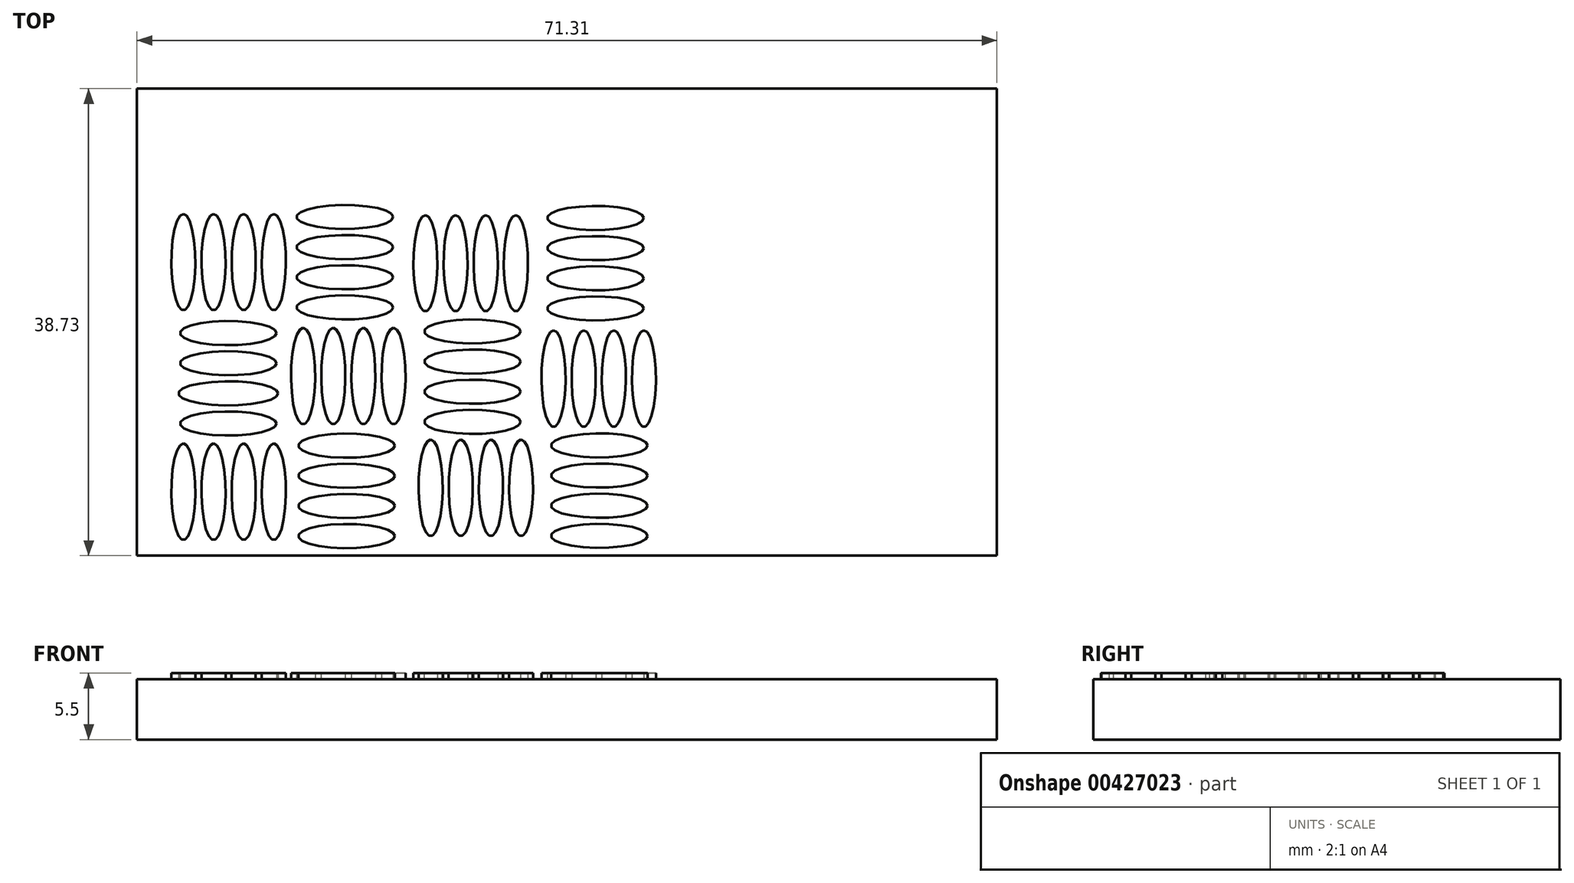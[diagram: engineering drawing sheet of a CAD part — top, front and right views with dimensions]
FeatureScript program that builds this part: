
annotation { "Feature Type Name" : "Feature", "Feature Type Description" : "" }
export const myFeature = defineFeature(function(context is Context, id is Id, definition is map)
    precondition{}
    {
        {
            var Q0;
            Q0=qCreatedBy(makeId("Top.planeOp"),FACE);
            var sketch = newSketch(context, id + "F0", { "sketchPlane" : qUnion([Q0])});
            skLineSegment(sketch, "E0.bottom", {"start": v(0, -0.64) * mm, "end": v(71.3, -0.64) * mm});
            skLineSegment(sketch, "E0.top", {"start": v(0, 38.1) * mm, "end": v(71.3, 38.1) * mm});
            skLineSegment(sketch, "E0.left", {"start": v(0, -0.64) * mm, "end": v(0, 38.1) * mm});
            skLineSegment(sketch, "E0.right", {"start": v(71.3, -0.64) * mm, "end": v(71.3, 38.1) * mm});
            skSolve(sketch);
        }
        {
            var Q0;
            Q0 = qSketchRegion(id + "F0", true);
            extrude(context, id + "F1", {"entities" : qUnion([Q0]), "depth" : 5 * mm});
        }
        {
            var Q0;
            Q0=makeQuery(id+"F1.opExtrude","CAP_FACE",FACE,{"disambiguationData":[OSD([sQuery(id+"F0.wireOp",EDGE,"E0.bottom"),sQuery(id+"F0.wireOp",EDGE,"E0.top"),sQuery(id+"F0.wireOp",EDGE,"E0.left"),sQuery(id+"F0.wireOp",EDGE,"E0.right")])],"isStart":false});
            var sketch = newSketch(context, id + "F2", { "sketchPlane" : qUnion([Q0])});
            skEllipse(sketch, "E1", {"center": v(3.85, 4.66) * mm, "majorRadius": 4 * mm, "minorRadius": 1 * mm, "majorAxis": v(0, 1)});
            skEllipse(sketch, "E2", {"center": v(6.35, 4.66) * mm, "majorRadius": 4 * mm, "minorRadius": 1 * mm, "majorAxis": v(0, 1)});
            skPoint(sketch, "E2.centerSnap0", {"position": v(4.85, 4.66) * mm});
            skEllipse(sketch, "E3", {"center": v(8.85, 4.66) * mm, "majorRadius": 4 * mm, "minorRadius": 1 * mm, "majorAxis": v(0, 1)});
            skEllipse(sketch, "E4", {"center": v(11.35, 4.66) * mm, "majorRadius": 4 * mm, "minorRadius": 1 * mm, "majorAxis": v(0, 1)});
            skEllipse(sketch, "E5", {"center": v(7.57, 10.32) * mm, "majorRadius": 4 * mm, "minorRadius": 1 * mm, "majorAxis": v(1, 0)});
            skEllipse(sketch, "E6", {"center": v(7.57, 12.82) * mm, "majorRadius": 4.13 * mm, "minorRadius": 1 * mm, "majorAxis": v(1, 0)});
            skEllipse(sketch, "E7", {"center": v(7.57, 15.32) * mm, "majorRadius": 4 * mm, "minorRadius": 1 * mm, "majorAxis": v(1, 0)});
            skEllipse(sketch, "E8", {"center": v(7.57, 17.82) * mm, "majorRadius": 4 * mm, "minorRadius": 1 * mm, "majorAxis": v(1, 0)});
            skPoint(sketch, "E8.centerSnap0", {"position": v(7.57, 16.32) * mm});
            skSolve(sketch);
        }
        {
            var Q0;
            Q0 = qSketchRegion(id + "F2", true);
            extrude(context, id + "F3", {"entities" : qUnion([Q0]), "operationType" : NewBodyOperationType.ADD, "depth" : 0.5 * mm});
        }
        {
            var Q0;
            Q0=makeQuery(id+"F1.opExtrude","CAP_FACE",FACE,{"disambiguationData":[OSD([sQuery(id+"F0.wireOp",EDGE,"E0.bottom"),sQuery(id+"F0.wireOp",EDGE,"E0.top"),sQuery(id+"F0.wireOp",EDGE,"E0.left"),sQuery(id+"F0.wireOp",EDGE,"E0.right")])],"isStart":false});
            var sketch = newSketch(context, id + "F4", { "sketchPlane" : qUnion([Q0])});
            skEllipse(sketch, "E9", {"center": v(3.85, 23.7) * mm, "majorRadius": 4 * mm, "minorRadius": 1 * mm, "majorAxis": v(0, 1)});
            skPoint(sketch, "E9.centerSnap0", {"position": v(3.85, 8.66) * mm});
            skEllipse(sketch, "E10", {"center": v(6.35, 23.7) * mm, "majorRadius": 4 * mm, "minorRadius": 1 * mm, "majorAxis": v(0, 1)});
            skPoint(sketch, "E10.centerSnap0", {"position": v(4.85, 23.7) * mm});
            skEllipse(sketch, "E11", {"center": v(8.85, 23.7) * mm, "majorRadius": 4 * mm, "minorRadius": 1 * mm, "majorAxis": v(0, 1)});
            skPoint(sketch, "E11.centerSnap0", {"position": v(7.35, 23.7) * mm});
            skEllipse(sketch, "E12", {"center": v(11.35, 23.7) * mm, "majorRadius": 4 * mm, "minorRadius": 1 * mm, "majorAxis": v(0, 1)});
            skEllipse(sketch, "E13", {"center": v(17.39, 0.99) * mm, "majorRadius": 4 * mm, "minorRadius": 1 * mm, "majorAxis": v(1, 0)});
            skEllipse(sketch, "E14", {"center": v(17.39, 3.49) * mm, "majorRadius": 4 * mm, "minorRadius": 1 * mm, "majorAxis": v(1, 0)});
            skEllipse(sketch, "E15", {"center": v(17.39, 5.99) * mm, "majorRadius": 4 * mm, "minorRadius": 1 * mm, "majorAxis": v(1, 0)});
            skEllipse(sketch, "E16", {"center": v(17.39, 8.49) * mm, "majorRadius": 4 * mm, "minorRadius": 1 * mm, "majorAxis": v(1, 0)});
            skEllipse(sketch, "E17", {"center": v(24.35, 4.99) * mm, "majorRadius": 4 * mm, "minorRadius": 1 * mm, "majorAxis": v(0, 1)});
            skPoint(sketch, "E17.centerSnap0", {"position": v(17.39, 4.99) * mm});
            skEllipse(sketch, "E18", {"center": v(26.85, 4.99) * mm, "majorRadius": 4 * mm, "minorRadius": 1 * mm, "majorAxis": v(0, 1)});
            skPoint(sketch, "E18.centerSnap0", {"position": v(25.35, 4.99) * mm});
            skEllipse(sketch, "E19", {"center": v(29.35, 4.99) * mm, "majorRadius": 4 * mm, "minorRadius": 1 * mm, "majorAxis": v(0, 1)});
            skEllipse(sketch, "E20", {"center": v(31.85, 4.99) * mm, "majorRadius": 4 * mm, "minorRadius": 1 * mm, "majorAxis": v(0, 1)});
            skPoint(sketch, "E20.centerSnap0", {"position": v(30.35, 4.99) * mm});
            skSolve(sketch);
        }
        {
            var Q0;
            Q0 = qSketchRegion(id + "F4", true);
            extrude(context, id + "F5", {"entities" : qUnion([Q0]), "operationType" : NewBodyOperationType.ADD, "depth" : 0.5 * mm});
        }
        {
            var Q0;
            Q0=makeQuery(id+"F1.opExtrude","CAP_FACE",FACE,{"disambiguationData":[OSD([sQuery(id+"F0.wireOp",EDGE,"E0.bottom"),sQuery(id+"F0.wireOp",EDGE,"E0.top"),sQuery(id+"F0.wireOp",EDGE,"E0.left"),sQuery(id+"F0.wireOp",EDGE,"E0.right")])],"isStart":false});
            var sketch = newSketch(context, id + "F6", { "sketchPlane" : qUnion([Q0])});
            skEllipse(sketch, "E21", {"center": v(13.78, 14.26) * mm, "majorRadius": 4 * mm, "minorRadius": 1 * mm, "majorAxis": v(0, 1)});
            skEllipse(sketch, "E22", {"center": v(16.28, 14.26) * mm, "majorRadius": 4 * mm, "minorRadius": 1 * mm, "majorAxis": v(0, 1)});
            skPoint(sketch, "E22.centerSnap0", {"position": v(14.78, 14.26) * mm});
            skEllipse(sketch, "E23", {"center": v(18.78, 14.26) * mm, "majorRadius": 4 * mm, "minorRadius": 1 * mm, "majorAxis": v(0, 1)});
            skPoint(sketch, "E23.centerSnap0", {"position": v(17.28, 14.26) * mm});
            skEllipse(sketch, "E24", {"center": v(21.28, 14.26) * mm, "majorRadius": 4 * mm, "minorRadius": 1 * mm, "majorAxis": v(0, 1)});
            skPoint(sketch, "E24.centerSnap0", {"position": v(19.78, 14.26) * mm});
            skSolve(sketch);
        }
        {
            var Q0;
            Q0 = qSketchRegion(id + "F6", true);
            extrude(context, id + "F7", {"entities" : qUnion([Q0]), "operationType" : NewBodyOperationType.ADD, "depth" : 0.5 * mm});
        }
        {
            var Q0;
            Q0=makeQuery(id+"F1.opExtrude","CAP_FACE",FACE,{"disambiguationData":[OSD([sQuery(id+"F0.wireOp",EDGE,"E0.bottom"),sQuery(id+"F0.wireOp",EDGE,"E0.top"),sQuery(id+"F0.wireOp",EDGE,"E0.left"),sQuery(id+"F0.wireOp",EDGE,"E0.right")])],"isStart":false});
            var sketch = newSketch(context, id + "F8", { "sketchPlane" : qUnion([Q0])});
            skEllipse(sketch, "E25", {"center": v(17.24, 19.95) * mm, "majorRadius": 4 * mm, "minorRadius": 1 * mm, "majorAxis": v(1, 0)});
            skEllipse(sketch, "E26", {"center": v(17.24, 22.45) * mm, "majorRadius": 4 * mm, "minorRadius": 1 * mm, "majorAxis": v(1, 0)});
            skEllipse(sketch, "E27", {"center": v(17.24, 24.95) * mm, "majorRadius": 4 * mm, "minorRadius": 1 * mm, "majorAxis": v(1, 0)});
            skPoint(sketch, "E27.centerSnap0", {"position": v(17.24, 23.45) * mm});
            skEllipse(sketch, "E28", {"center": v(17.24, 27.45) * mm, "majorRadius": 4 * mm, "minorRadius": 1 * mm, "majorAxis": v(1, 0)});
            skPoint(sketch, "E28.centerSnap0", {"position": v(17.24, 25.95) * mm});
            skSolve(sketch);
        }
        {
            var Q0;
            Q0 = qSketchRegion(id + "F8", true);
            extrude(context, id + "F9", {"entities" : qUnion([Q0]), "operationType" : NewBodyOperationType.ADD, "depth" : 0.5 * mm});
        }
        {
            var Q0;
            Q0=makeQuery(id+"F1.opExtrude","CAP_FACE",FACE,{"disambiguationData":[OSD([sQuery(id+"F0.wireOp",EDGE,"E0.bottom"),sQuery(id+"F0.wireOp",EDGE,"E0.top"),sQuery(id+"F0.wireOp",EDGE,"E0.left"),sQuery(id+"F0.wireOp",EDGE,"E0.right")])],"isStart":false});
            var sketch = newSketch(context, id + "F10", { "sketchPlane" : qUnion([Q0])});
            skEllipse(sketch, "E29", {"center": v(27.81, 10.46) * mm, "majorRadius": 4 * mm, "minorRadius": 1 * mm, "majorAxis": v(1, 0)});
            skEllipse(sketch, "E30", {"center": v(27.81, 12.96) * mm, "majorRadius": 4 * mm, "minorRadius": 1 * mm, "majorAxis": v(1, 0)});
            skPoint(sketch, "E30.centerSnap0", {"position": v(27.81, 11.46) * mm});
            skEllipse(sketch, "E31", {"center": v(27.81, 15.46) * mm, "majorRadius": 4 * mm, "minorRadius": 1 * mm, "majorAxis": v(1, 0)});
            skPoint(sketch, "E31.centerSnap0", {"position": v(27.81, 13.96) * mm});
            skEllipse(sketch, "E32", {"center": v(27.81, 17.96) * mm, "majorRadius": 4 * mm, "minorRadius": 1 * mm, "majorAxis": v(1, 0)});
            skPoint(sketch, "E32.centerSnap0", {"position": v(27.81, 16.46) * mm});
            skSolve(sketch);
        }
        {
            var Q0;
            Q0 = qSketchRegion(id + "F10", true);
            extrude(context, id + "F11", {"entities" : qUnion([Q0]), "operationType" : NewBodyOperationType.ADD, "depth" : 0.5 * mm});
        }
        {
            var Q0;
            Q0=makeQuery(id+"F1.opExtrude","CAP_FACE",FACE,{"disambiguationData":[OSD([sQuery(id+"F0.wireOp",EDGE,"E0.bottom"),sQuery(id+"F0.wireOp",EDGE,"E0.top"),sQuery(id+"F0.wireOp",EDGE,"E0.left"),sQuery(id+"F0.wireOp",EDGE,"E0.right")])],"isStart":false});
            var sketch = newSketch(context, id + "F12", { "sketchPlane" : qUnion([Q0])});
            skEllipse(sketch, "E33", {"center": v(23.92, 23.6) * mm, "majorRadius": 4 * mm, "minorRadius": 1 * mm, "majorAxis": v(0, 1)});
            skEllipse(sketch, "E34", {"center": v(26.42, 23.6) * mm, "majorRadius": 4 * mm, "minorRadius": 1 * mm, "majorAxis": v(0, 1)});
            skPoint(sketch, "E34.centerSnap0", {"position": v(24.92, 23.6) * mm});
            skEllipse(sketch, "E35", {"center": v(28.92, 23.6) * mm, "majorRadius": 4 * mm, "minorRadius": 1 * mm, "majorAxis": v(0, 1)});
            skPoint(sketch, "E35.centerSnap0", {"position": v(27.42, 23.6) * mm});
            skEllipse(sketch, "E36", {"center": v(31.42, 23.6) * mm, "majorRadius": 4 * mm, "minorRadius": 1 * mm, "majorAxis": v(0, 1)});
            skPoint(sketch, "E36.centerSnap0", {"position": v(29.92, 23.6) * mm});
            skSolve(sketch);
        }
        {
            var Q0;
            Q0 = qSketchRegion(id + "F12", true);
            extrude(context, id + "F13", {"entities" : qUnion([Q0]), "operationType" : NewBodyOperationType.ADD, "depth" : 0.5 * mm});
        }
        {
            var Q0;
            Q0=makeQuery(id+"F1.opExtrude","CAP_FACE",FACE,{"disambiguationData":[OSD([sQuery(id+"F0.wireOp",EDGE,"E0.bottom"),sQuery(id+"F0.wireOp",EDGE,"E0.top"),sQuery(id+"F0.wireOp",EDGE,"E0.left"),sQuery(id+"F0.wireOp",EDGE,"E0.right")])],"isStart":false});
            var sketch = newSketch(context, id + "F14", { "sketchPlane" : qUnion([Q0])});
            skEllipse(sketch, "E37", {"center": v(38.34, 1) * mm, "majorRadius": 4 * mm, "minorRadius": 1 * mm, "majorAxis": v(1, 0)});
            skEllipse(sketch, "E38", {"center": v(38.34, 3.5) * mm, "majorRadius": 4 * mm, "minorRadius": 1 * mm, "majorAxis": v(1, 0)});
            skPoint(sketch, "E38.centerSnap0", {"position": v(38.34, 2) * mm});
            skEllipse(sketch, "E39", {"center": v(38.34, 6) * mm, "majorRadius": 4 * mm, "minorRadius": 1 * mm, "majorAxis": v(1, 0)});
            skPoint(sketch, "E39.centerSnap0", {"position": v(38.34, 4.5) * mm});
            skEllipse(sketch, "E40", {"center": v(38.34, 8.5) * mm, "majorRadius": 4 * mm, "minorRadius": 1 * mm, "majorAxis": v(1, 0)});
            skPoint(sketch, "E40.centerSnap0", {"position": v(38.34, 7) * mm});
            skSolve(sketch);
        }
        {
            var Q0;
            Q0 = qSketchRegion(id + "F14", true);
            extrude(context, id + "F15", {"entities" : qUnion([Q0]), "operationType" : NewBodyOperationType.ADD, "depth" : 0.5 * mm});
        }
        {
            var Q0;
            Q0=makeQuery(id+"F1.opExtrude","CAP_FACE",FACE,{"disambiguationData":[OSD([sQuery(id+"F0.wireOp",EDGE,"E0.bottom"),sQuery(id+"F0.wireOp",EDGE,"E0.top"),sQuery(id+"F0.wireOp",EDGE,"E0.left"),sQuery(id+"F0.wireOp",EDGE,"E0.right")])],"isStart":false});
            var sketch = newSketch(context, id + "F16", { "sketchPlane" : qUnion([Q0])});
            skEllipse(sketch, "E41", {"center": v(34.54, 14.05) * mm, "majorRadius": 4 * mm, "minorRadius": 1 * mm, "majorAxis": v(0, 1)});
            skEllipse(sketch, "E42", {"center": v(37.04, 14.05) * mm, "majorRadius": 4 * mm, "minorRadius": 1 * mm, "majorAxis": v(0, 1)});
            skPoint(sketch, "E42.centerSnap0", {"position": v(35.54, 14.05) * mm});
            skEllipse(sketch, "E43", {"center": v(39.54, 14.05) * mm, "majorRadius": 4 * mm, "minorRadius": 1 * mm, "majorAxis": v(0, 1)});
            skPoint(sketch, "E43.centerSnap0", {"position": v(38.04, 14.05) * mm});
            skEllipse(sketch, "E44", {"center": v(42.04, 14.05) * mm, "majorRadius": 4 * mm, "minorRadius": 1 * mm, "majorAxis": v(0, 1)});
            skPoint(sketch, "E44.centerSnap0", {"position": v(40.54, 14.05) * mm});
            skSolve(sketch);
        }
        {
            var Q0;
            Q0 = qSketchRegion(id + "F16", true);
            extrude(context, id + "F17", {"entities" : qUnion([Q0]), "operationType" : NewBodyOperationType.ADD, "depth" : 0.5 * mm});
        }
        {
            var Q0;
            Q0=makeQuery(id+"F1.opExtrude","CAP_FACE",FACE,{"disambiguationData":[OSD([sQuery(id+"F0.wireOp",EDGE,"E0.bottom"),sQuery(id+"F0.wireOp",EDGE,"E0.top"),sQuery(id+"F0.wireOp",EDGE,"E0.left"),sQuery(id+"F0.wireOp",EDGE,"E0.right")])],"isStart":false});
            var sketch = newSketch(context, id + "F18", { "sketchPlane" : qUnion([Q0])});
            skEllipse(sketch, "E45", {"center": v(38.02, 19.87) * mm, "majorRadius": 4 * mm, "minorRadius": 1 * mm, "majorAxis": v(1, 0)});
            skEllipse(sketch, "E46", {"center": v(38.02, 22.37) * mm, "majorRadius": 4 * mm, "minorRadius": 1 * mm, "majorAxis": v(1, 0)});
            skPoint(sketch, "E46.centerSnap0", {"position": v(38.02, 20.87) * mm});
            skEllipse(sketch, "E47", {"center": v(38.02, 24.87) * mm, "majorRadius": 4 * mm, "minorRadius": 1 * mm, "majorAxis": v(1, 0)});
            skPoint(sketch, "E47.centerSnap0", {"position": v(38.02, 23.37) * mm});
            skEllipse(sketch, "E48", {"center": v(38.02, 27.37) * mm, "majorRadius": 4 * mm, "minorRadius": 1 * mm, "majorAxis": v(1, 0)});
            skPoint(sketch, "E48.centerSnap0", {"position": v(38.02, 25.87) * mm});
            skSolve(sketch);
        }
        {
            var Q0;
            Q0 = qSketchRegion(id + "F18", true);
            extrude(context, id + "F19", {"entities" : qUnion([Q0]), "operationType" : NewBodyOperationType.ADD, "depth" : 0.5 * mm});
        }
    });
